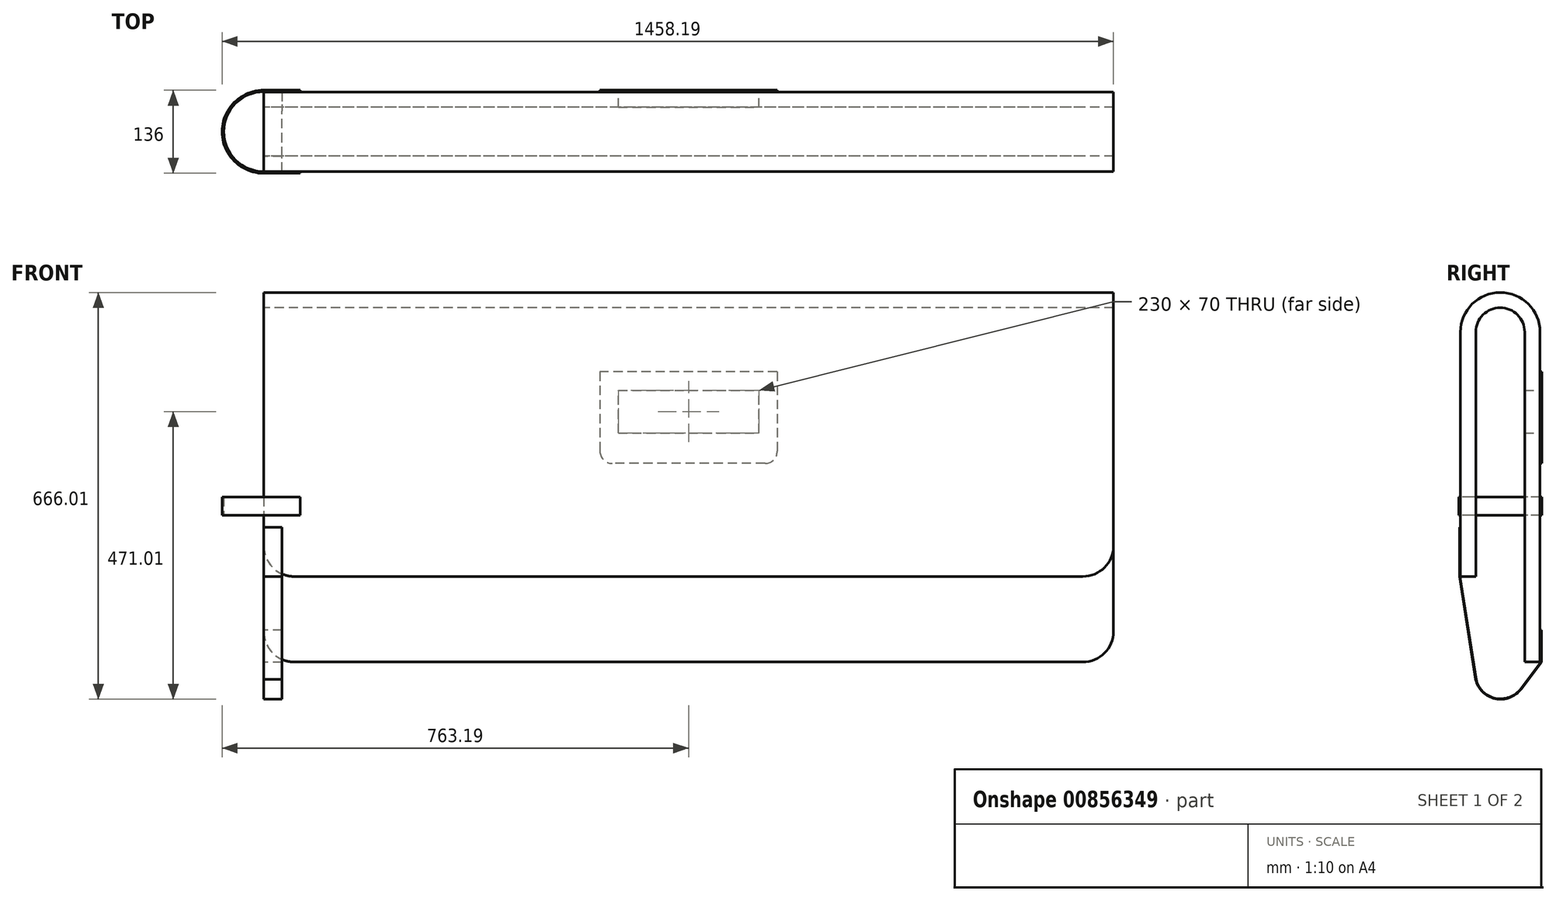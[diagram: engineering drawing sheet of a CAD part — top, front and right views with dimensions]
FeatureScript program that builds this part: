
annotation { "Feature Type Name" : "Feature", "Feature Type Description" : "" }
export const myFeature = defineFeature(function(context is Context, id is Id, definition is map)
    precondition{}
    {
        {
            var Q0;
            Q0=qCreatedBy(makeId("Right.planeOp"),FACE);
            var sketch = newSketch(context, id + "F0", { "sketchPlane" : qUnion([Q0])});
            skLineSegment(sketch, "E0", {"start": v(-65, 0) * mm, "end": v(-65, -400) * mm});
            skLineSegment(sketch, "E1", {"start": v(-40, 0) * mm, "end": v(-40, -400) * mm});
            skLineSegment(sketch, "E2", {"start": v(-40, -400) * mm, "end": v(-65, -400) * mm});
            skLineSegment(sketch, "E3", {"start": v(65, 0) * mm, "end": v(65, -540) * mm});
            skLineSegment(sketch, "E4", {"start": v(40, 0) * mm, "end": v(40, -540) * mm});
            skLineSegment(sketch, "E5", {"start": v(40, -540) * mm, "end": v(65, -540) * mm});
            skArc(sketch, "E6", {"start": v(40, 0) * mm, "mid": v(0, 40) * mm, "end": v(-40, 0) * mm});
            skArc(sketch, "E7", {"start": v(65, 0) * mm, "mid": v(0, 65) * mm, "end": v(-65, 0) * mm});
            skLineSegment(sketch, "E8", {"start": v(66.4, -487.5) * mm, "end": v(66.4, -540.55) * mm});
            skLineSegment(sketch, "E9", {"start": v(66.4, -540.55) * mm, "end": v(33.62, -583.87) * mm});
            skLineSegment(sketch, "E10", {"start": v(67.59, -487.5) * mm, "end": v(67.59, -540.55) * mm});
            skLineSegment(sketch, "E11", {"start": v(67.59, -540.55) * mm, "end": v(34.16, -584.44) * mm});
            skLineSegment(sketch, "E12", {"start": v(-65.7, -319.78) * mm, "end": v(-65.7, -400.2) * mm});
            skLineSegment(sketch, "E13", {"start": v(-65.7, -400.2) * mm, "end": v(-39.5, -568.5) * mm});
            skLineSegment(sketch, "E14", {"start": v(-65.7, -319.78) * mm, "end": v(-66.76, -319.78) * mm});
            skLineSegment(sketch, "E15", {"start": v(-66.76, -319.78) * mm, "end": v(-66.76, -400.12) * mm});
            skLineSegment(sketch, "E16", {"start": v(-66.76, -400.12) * mm, "end": v(-40.27, -568.53) * mm});
            skArc(sketch, "E17", {"start": v(-39.5, -568.5) * mm, "mid": v(-7.81, -599.36) * mm, "end": v(33.62, -583.87) * mm});
            skArc(sketch, "E18", {"start": v(-40.27, -568.53) * mm, "mid": v(-8.1, -600.08) * mm, "end": v(34.16, -584.44) * mm});
            skLineSegment(sketch, "E19", {"start": v(66.4, -487.5) * mm, "end": v(67.59, -487.5) * mm});
            skSolve(sketch);
        }
        {
            var Q0;
            Q0=makeQuery(id+"F0.imprint","IMPRINT",FACE,{"disambiguationData":[TD([[makeQuery(id+"F0.imprint","IMPRINT",EDGE,{"derivedFrom":sQuery(id+"F0.wireOp",EDGE,"E0")}),1.0]])]});
            extrude(context, id + "F1", {"entities" : qUnion([Q0]), "depth" : 1390 * mm, "offsetDistance" : 25 * mm});
        }
        {
            var Q0;
            Q0=makeQuery(id+"F1.opExtrude","SWEPT_FACE",FACE,{"disambiguationData":[OSD([sQuery(id+"F0.wireOp",EDGE,"E3")])]});
            var sketch = newSketch(context, id + "F2", { "sketchPlane" : qUnion([Q0])});
            skLineSegment(sketch, "E20.bottom", {"start": v(-810, -95) * mm, "end": v(-580, -95) * mm});
            skLineSegment(sketch, "E20.top", {"start": v(-810, -165) * mm, "end": v(-580, -165) * mm});
            skLineSegment(sketch, "E20.left", {"start": v(-810, -95) * mm, "end": v(-810, -165) * mm});
            skLineSegment(sketch, "E20.right", {"start": v(-580, -95) * mm, "end": v(-580, -165) * mm});
            skSolve(sketch);
        }
        {
            var Q0;
            Q0=makeQuery(id+"F2.imprint","IMPRINT",FACE,{"disambiguationData":[TD([[makeQuery(id+"F2.imprint","IMPRINT",EDGE,{"derivedFrom":sQuery(id+"F2.wireOp",EDGE,"E20.bottom")}),-1.0]])]});
            extrude(context, id + "F3", {"entities" : qUnion([Q0]), "operationType" : NewBodyOperationType.REMOVE, "endBound" : BoundingType.UP_TO_NEXT, "oppositeDirection" : true, "depth" : 25 * mm, "offsetDistance" : 25 * mm});
        }
        {
            var Q0;
            Q0=makeQuery(id+"F1.opExtrude","CAP_EDGE",EDGE,{"disambiguationData":[OSD([sQuery(id+"F0.wireOp",EDGE,"E5")])],"isStart":false});
            var Q1;
            Q1=makeQuery(id+"F1.opExtrude","CAP_EDGE",EDGE,{"disambiguationData":[OSD([sQuery(id+"F0.wireOp",EDGE,"E5")])],"isStart":true});
            var Q2;
            Q2=makeQuery(id+"F1.opExtrude","CAP_EDGE",EDGE,{"disambiguationData":[OSD([sQuery(id+"F0.wireOp",EDGE,"E2")])],"isStart":true});
            var Q3;
            Q3=makeQuery(id+"F1.opExtrude","CAP_EDGE",EDGE,{"disambiguationData":[OSD([sQuery(id+"F0.wireOp",EDGE,"E2")])],"isStart":false});
            fillet(context, id + "F4", {"entities" : qUnion([Q0, Q1, Q2, Q3]), "radius" : 50 * mm, "tangentPropagation" : true, "allowEdgeOverflow" : false});
        }
        {
            var Q0;
            Q0=makeQuery(id+"F0.imprint","IMPRINT",FACE,{"disambiguationData":[TD([[makeQuery(id+"F0.imprint","IMPRINT",EDGE,{"derivedFrom":sQuery(id+"F0.wireOp",EDGE,"E8")}),1.0]])]});
            extrude(context, id + "F5", {"entities" : qUnion([Q0]), "depth" : 30 * mm, "offsetDistance" : 25 * mm});
        }
        {
            var Q0;
            Q0=qCreatedBy(makeId("Top.planeOp"),FACE);
            cPlane(context, id + "F6", {"entities" : qUnion([Q0]), "cplaneType" : CPlaneType.OFFSET, "offset" : 300 * mm, "oppositeDirection" : true, "width" : 150 * mm, "height" : 150 * mm});
        }
        {
            var Q0;
            Q0=qCreatedBy(id+"F6.planeOp",FACE);
            var sketch = newSketch(context, id + "F7", { "sketchPlane" : qUnion([Q0])});
            skLineSegment(sketch, "E21", {"start": v(59.28, 68) * mm, "end": v(0, 68) * mm});
            skLineSegment(sketch, "E22", {"start": v(59.28, -68) * mm, "end": v(0, -68) * mm});
            skArc(sketch, "E23", {"start": v(0, 68) * mm, "mid": v(-68.19, 0) * mm, "end": v(0, -68) * mm});
            skLineSegment(sketch, "E24", {"start": v(59.28, 68) * mm, "end": v(59.28, 65.64) * mm});
            skLineSegment(sketch, "E25", {"start": v(59.28, 65.64) * mm, "end": v(0, 65.64) * mm});
            skLineSegment(sketch, "E26", {"start": v(59.28, -68) * mm, "end": v(59.28, -65.26) * mm});
            skLineSegment(sketch, "E27", {"start": v(59.28, -65.26) * mm, "end": v(0, -65.26) * mm});
            skArc(sketch, "E28", {"start": v(0, 65.64) * mm, "mid": v(-65.45, 0.19) * mm, "end": v(0, -65.26) * mm});
            skSolve(sketch);
        }
        {
            var Q0;
            Q0=makeQuery(id+"F7.imprint","IMPRINT",FACE,{"disambiguationData":[TD([[makeQuery(id+"F7.imprint","IMPRINT",EDGE,{"derivedFrom":sQuery(id+"F7.wireOp",EDGE,"E21")}),1.0]])]});
            extrude(context, id + "F8", {"entities" : qUnion([Q0]), "depth" : 30 * mm, "offsetDistance" : 25 * mm});
        }
        {
            var Q0;
            Q0=makeQuery(id+"F1.opExtrude","SWEPT_FACE",FACE,{"disambiguationData":[OSD([sQuery(id+"F0.wireOp",EDGE,"E3")])]});
            var sketch = newSketch(context, id + "F9", { "sketchPlane" : qUnion([Q0])});
            skLineSegment(sketch, "E29.bottom", {"start": v(-840, -65) * mm, "end": v(-550, -65) * mm});
            skLineSegment(sketch, "E29.top", {"start": v(-840, -215) * mm, "end": v(-550, -215) * mm});
            skLineSegment(sketch, "E29.left", {"start": v(-840, -65) * mm, "end": v(-840, -215) * mm});
            skLineSegment(sketch, "E29.right", {"start": v(-550, -65) * mm, "end": v(-550, -215) * mm});
            skSolve(sketch);
        }
        {
            var Q0;
            Q0=makeQuery(id+"F9.imprint","IMPRINT",FACE,{"disambiguationData":[TD([[makeQuery(id+"F9.imprint","IMPRINT",EDGE,{"derivedFrom":sQuery(id+"F9.wireOp",EDGE,"E29.bottom")}),-1.0]])]});
            var Q1;
            Q1=makeQuery(id+"F9.imprint","IMPRINT",FACE,{"disambiguationData":[TD([[makeQuery(id+"F9.imprint","IMPRINT",EDGE,{"derivedFrom":makeQuery(id+"F3.boolean.opBoolean","COPY",EDGE,{"derivedFrom":makeQuery(id+"F3.opExtrude","CAP_EDGE",EDGE,{"disambiguationData":[OSD([sQuery(id+"F2.wireOp",EDGE,"E20.bottom")])],"isStart":true})})}),-1.0]])]});
            extrude(context, id + "F10", {"entities" : qUnion([Q0, Q1]), "operationType" : NewBodyOperationType.ADD, "depth" : 3 * mm, "offsetDistance" : 25 * mm});
        }
        {
            var Q0;
            Q0=makeQuery(id+"F10.opExtrude","SWEPT_EDGE",EDGE,{"disambiguationData":[OSD([sQuery(id+"F9.wireOp",EDGE,"E29.top"),sQuery(id+"F9.wireOp",EDGE,"E29.left")])]});
            var Q1;
            Q1=makeQuery(id+"F10.opExtrude","SWEPT_EDGE",EDGE,{"disambiguationData":[OSD([sQuery(id+"F9.wireOp",EDGE,"E29.top"),sQuery(id+"F9.wireOp",EDGE,"E29.right")])]});
            fillet(context, id + "F11", {"entities" : qUnion([Q0, Q1]), "radius" : 20 * mm, "tangentPropagation" : true, "allowEdgeOverflow" : false});
        }
    });
